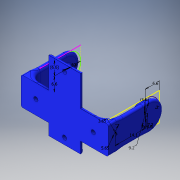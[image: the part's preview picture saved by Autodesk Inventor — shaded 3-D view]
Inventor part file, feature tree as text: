
AUTODESK INVENTOR PART (.ipt)
format: ipt  version: 2016 (Build 200138000, 138)  size: 482,816 bytes
history: native  units: in
note: dims shown in document units (in); Inventor stores cm internally (conversion verified against a paired STEP export)
features: fillet x10, extrude x9, sketch x9, hole x1
ambient origin geometry x8: Origin, YZ Plane, XZ Plane, XY Plane, X Axis, Y Axis, Z Axis, Center Point
bodies: Solid1 (feature_tree)
feature tree (29):
  extrude  "Extrusion1"  Depth=0.5197in
  extrude  "Extrusion3"  Depth=0.0787in
  sketch  "Sketch5"  dims[d9=0.9449in d10=0.0in d11=0.2835in]
  extrude  "Extrusion4"  Depth=0.2835in
  extrude  "Extrusion5"  Depth=0.2598in
  fillet  "Fillet1"  Radius=0.2598in
  fillet  "Fillet4"  Radius=0.5197in
  fillet  "Fillet5"  Radius=0.3622in
  fillet  "Fillet6"  Radius=0.1437in
  fillet  "Fillet7"  Radius=0.5551in
  extrude  "Extrusion6"  Depth=0.0787in TaperAngle=0.0deg
  fillet  "Fillet8"  Radius=0.0787in
  sketch  "Sketch9"  dims[d19=0.2224in d24=0.0787in d25=0.0in d26=0.0787in]
  extrude  "Extrusion7"  Depth=0.0787in TaperAngle=0.0deg
  fillet  "Fillet10"  Radius=0.1969in
  fillet  "Fillet11"  Radius=0.0394in
  sketch  "Sketch10"  dims[d27=0.0787in d28=0.0787in d29=0.0in d30=0.1969in d33=0.0394in]
  extrude  "Extrusion8"  Depth=0.0394in
  extrude  "Extrusion10"  Depth=0.0787in
  extrude  "Extrusion11"  Depth=0.0354in
  hole  "Hole2"  [1 undecoded]
  fillet  "Fillet15"  Radius=0.2598in
  fillet  "Fillet16"  Radius=0.2598in
  sketch  "Sketch1"  dims[d0=1.6142in d1=0.5197in]
  sketch  "Sketch4"  dims[d2=0.0787in d3=0.0in d8=0.0787in]
  sketch  "Sketch7"  dims[d12=0.2598in d13=0.2598in d14=0.2598in d15=0.5197in d16=0.3622in d17=0.1437in d18=0.5551in]
  sketch  "Sketch15"  dims[d34=0.0394in d35=0.0394in]
  sketch  "Sketch16"  dims[d36=0.0197in d37=0.0787in]
  sketch  "Sketch17"  dims[d38=0.9449in d39=0.0in d40=0.1969in d43=0.2598in d44=0.2598in d45=0.2598in d46=0.1181in d47=0.1181in d48=0.0in d49=0.0394in d50=0.0394in d51=0.1181in d52=0.1181in d53=0.0in d79=0.5118in d80=0.5118in d81=0.2096in d82=0.0in d83=0.5118in d84=0.5118in d85=0.562in d86=0.0in d87=0.2953in d88=0.2953in d89=0.2598in d90=0.2598in d91=0.2756in d92=0.1181in d93=0.2953in d94=0.2953in d95=0.1181in d96=0.2598in d97=0.2598in d98=0.2756in d99=0.0787in d100=0.2362in d101=0.1575in d102=0.0787in d103=90.0deg d104=0.1181in d105=0.8108in d106=0.0748in d107=0.0354in]
note: 1 required parameter value undecoded (feature->parameter linkage not recoverable at this tier; creation-order binding heuristic only, values carry confidence <= 0.55)
